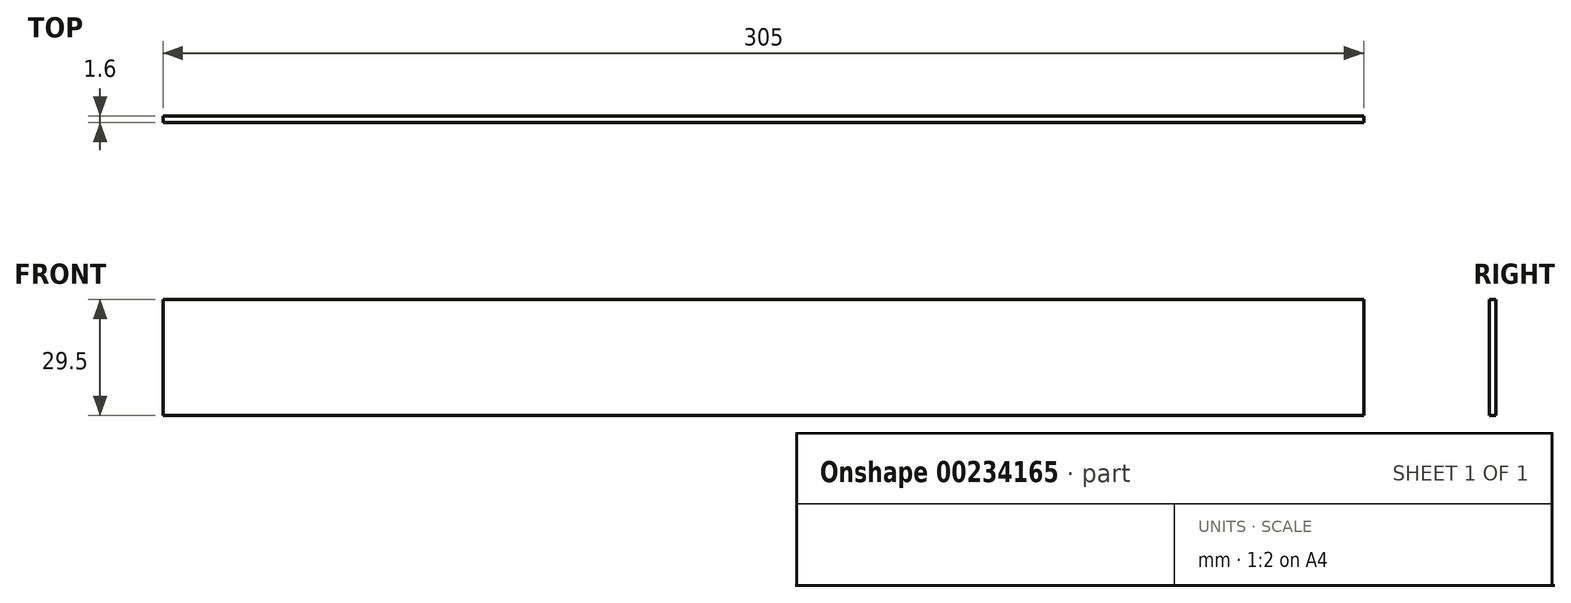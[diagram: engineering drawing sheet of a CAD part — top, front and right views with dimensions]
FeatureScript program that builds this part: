
annotation { "Feature Type Name" : "Feature", "Feature Type Description" : "" }
export const myFeature = defineFeature(function(context is Context, id is Id, definition is map)
    precondition{}
    {
        {
            var Q0;
            Q0=qCreatedBy(makeId("Front.planeOp"),FACE);
            var sketch = newSketch(context, id + "F0", { "sketchPlane" : qUnion([Q0])});
            skLineSegment(sketch, "E0.bottom", {"start": v(152.5, -14.75) * mm, "end": v(-152.5, -14.75) * mm});
            skLineSegment(sketch, "E0.top", {"start": v(152.5, 14.75) * mm, "end": v(-152.5, 14.75) * mm});
            skLineSegment(sketch, "E0.left", {"start": v(152.5, -14.75) * mm, "end": v(152.5, 14.75) * mm});
            skLineSegment(sketch, "E0.right", {"start": v(-152.5, -14.75) * mm, "end": v(-152.5, 14.75) * mm});
            skPoint(sketch, "E0.middle", {"position": v(0, 0) * mm});
            skSolve(sketch);
        }
        {
            var Q0;
            Q0=makeQuery(id+"F0.imprint","IMPRINT",FACE,{"disambiguationData":[TD([[makeQuery(id+"F0.imprint","IMPRINT",EDGE,{"derivedFrom":sQuery(id+"F0.wireOp",EDGE,"E0.bottom")}),-1.0]])]});
            extrude(context, id + "F1", {"entities" : qUnion([Q0]), "depth" : 1.6 * mm});
        }
    });
